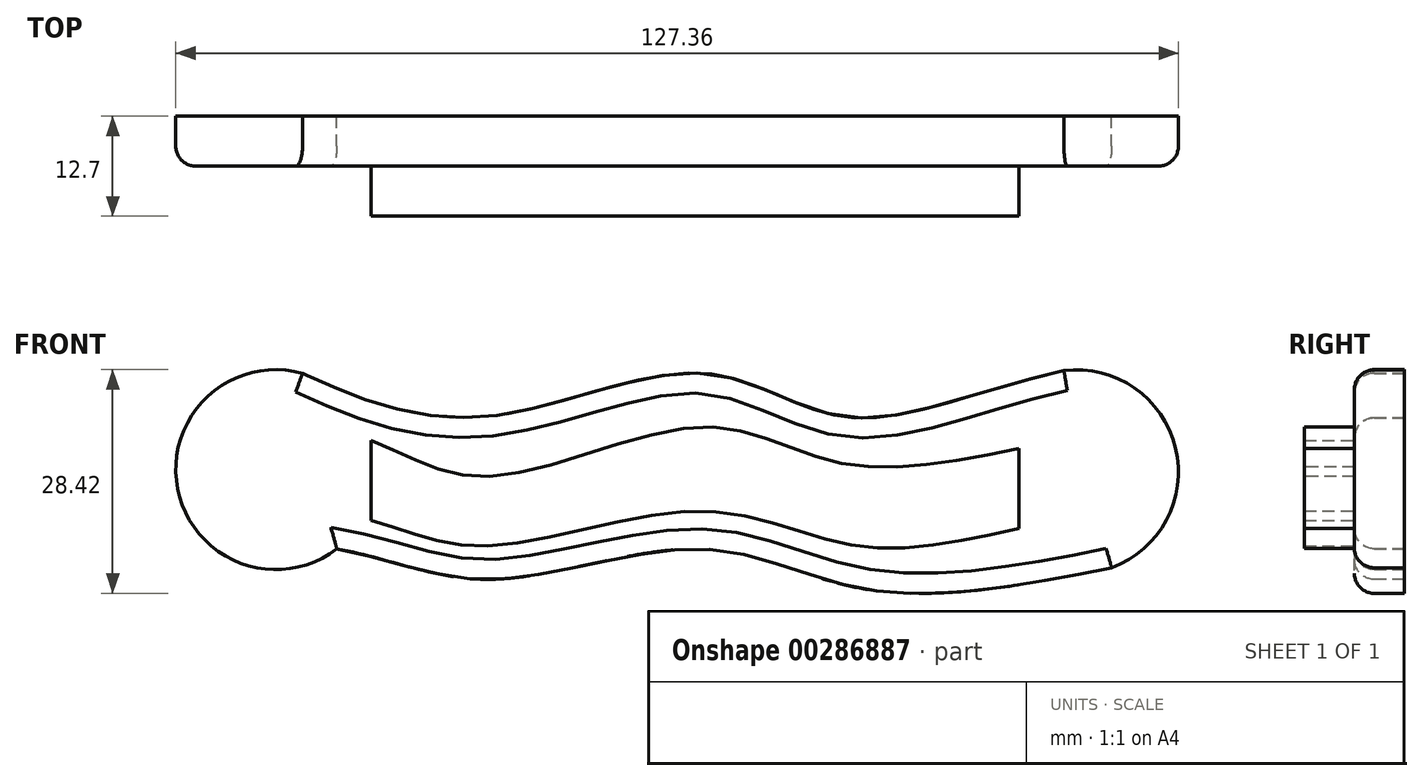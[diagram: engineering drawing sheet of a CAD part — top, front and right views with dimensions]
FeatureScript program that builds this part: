
annotation { "Feature Type Name" : "Feature", "Feature Type Description" : "" }
export const myFeature = defineFeature(function(context is Context, id is Id, definition is map)
    precondition{}
    {
        {
            var Q0;
            Q0=qCreatedBy(makeId("Front.planeOp"),FACE);
            var sketch = newSketch(context, id + "F0", { "sketchPlane" : qUnion([Q0])});
            skArc(sketch, "E0", {"start": v(-50.8, 40.74) * mm, "mid": v(-66.66, 26.08) * mm, "end": v(-46.45, 18.44) * mm});
            skArc(sketch, "E1", {"start": v(51.99, 16.04) * mm, "mid": v(60.1, 31.26) * mm, "end": v(45.92, 41.08) * mm});
            skFitSpline(sketch, "E2", {"points": [v(-50.8, 40.74) * mm, v(-27.84, 35.21) * mm, v(0, 40.74) * mm, v(18.07, 35.21) * mm, v(45.92, 41.08) * mm], "startDerivative": vector(86.64, -40.41) * mm, "endDerivative": vector(132.24, 29.83) * mm});
            skFitSpline(sketch, "E3", {"points": [v(-46.45, 18.44) * mm, v(-27.05, 14.56) * mm, v(0, 18.44) * mm, v(21.02, 13.27) * mm, v(51.99, 16.04) * mm], "startDerivative": vector(92.72, -15.8) * mm, "endDerivative": vector(110.17, 22.78) * mm});
            skLineSegment(sketch, "E4", {"start": v(-42.06, 32.23) * mm, "end": v(-42.06, 22.07) * mm});
            skLineSegment(sketch, "E5", {"start": v(40.19, 31.18) * mm, "end": v(40.19, 21.02) * mm});
            skFitSpline(sketch, "E6", {"points": [v(-42.06, 32.23) * mm, v(-27.1, 27.64) * mm, v(0, 33.92) * mm, v(17.7, 29.31) * mm, v(40.19, 31.18) * mm], "startDerivative": vector(65.05, -26.22) * mm, "endDerivative": vector(91.35, 18.2) * mm});
            skFitSpline(sketch, "E7", {"points": [v(-42.06, 22.07) * mm, v(-27.84, 18.8) * mm, v(0, 23.23) * mm, v(19.73, 18.8) * mm, v(40.19, 21.02) * mm], "startDerivative": vector(63.23, -16.78) * mm, "endDerivative": vector(84.32, 18.73) * mm});
            skSolve(sketch);
        }
        {
            var Q0;
            Q0=makeQuery(id+"F0.imprint","IMPRINT",FACE,{"disambiguationData":[TD([[makeQuery(id+"F0.imprint","IMPRINT",EDGE,{"derivedFrom":sQuery(id+"F0.wireOp",EDGE,"E0")}),1.0]])]});
            extrude(context, id + "F1", {"entities" : qUnion([Q0]), "depth" : 6.35 * mm});
        }
        {
            var Q0;
            Q0=makeQuery(id+"F0.imprint","IMPRINT",FACE,{"disambiguationData":[TD([[makeQuery(id+"F0.imprint","IMPRINT",EDGE,{"derivedFrom":sQuery(id+"F0.wireOp",EDGE,"E4")}),1.0]])]});
            extrude(context, id + "F2", {"entities" : qUnion([Q0]), "operationType" : NewBodyOperationType.ADD, "depth" : 12.7 * mm});
        }
        {
            var Q0;
            Q0=makeQuery(id+"F1.opExtrude","CAP_EDGE",EDGE,{"disambiguationData":[OSD([sQuery(id+"F0.wireOp",EDGE,"E0")])],"isStart":false});
            var Q1;
            Q1=makeQuery(id+"F1.opExtrude","CAP_EDGE",EDGE,{"disambiguationData":[OSD([sQuery(id+"F0.wireOp",EDGE,"E2")])],"isStart":false});
            var Q2;
            Q2=makeQuery(id+"F1.opExtrude","CAP_EDGE",EDGE,{"disambiguationData":[OSD([sQuery(id+"F0.wireOp",EDGE,"E3")])],"isStart":false});
            var Q3;
            Q3=makeQuery(id+"F1.opExtrude","CAP_EDGE",EDGE,{"disambiguationData":[OSD([sQuery(id+"F0.wireOp",EDGE,"E1")])],"isStart":false});
            fillet(context, id + "F3", {"entities" : qUnion([Q0, Q1, Q2, Q3]), "radius" : 2.54 * mm, "tangentPropagation" : true, "allowEdgeOverflow" : false});
        }
    });
